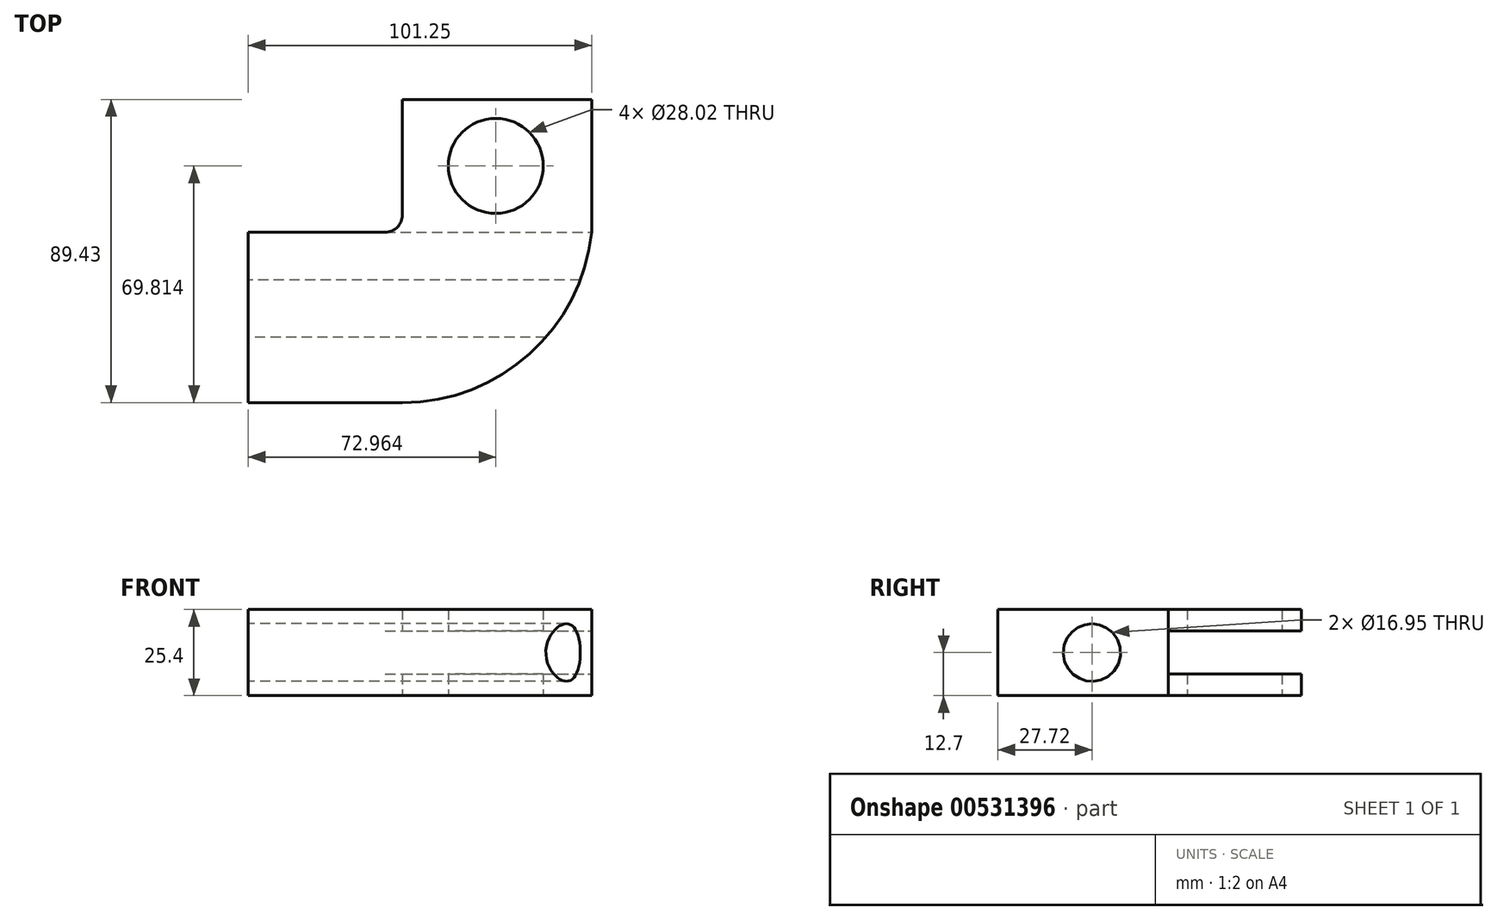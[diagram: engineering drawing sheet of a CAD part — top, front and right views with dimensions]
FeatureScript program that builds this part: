
annotation { "Feature Type Name" : "Feature", "Feature Type Description" : "" }
export const myFeature = defineFeature(function(context is Context, id is Id, definition is map)
    precondition{}
    {
        {
            var Q0;
            Q0=qCreatedBy(makeId("Top.planeOp"),FACE);
            var sketch = newSketch(context, id + "F0", { "sketchPlane" : qUnion([Q0])});
            skLineSegment(sketch, "E0.bottom", {"start": v(-45.45, 22.54) * mm, "end": v(0, 22.54) * mm});
            skLineSegment(sketch, "E0.top", {"start": v(-45.45, -27.72) * mm, "end": v(0, -27.72) * mm});
            skLineSegment(sketch, "E0.left", {"start": v(-45.45, 22.54) * mm, "end": v(-45.45, -27.72) * mm});
            skLineSegment(sketch, "E1.top", {"start": v(0, 61.71) * mm, "end": v(55.8, 61.71) * mm});
            skLineSegment(sketch, "E1.left", {"start": v(0, 22.54) * mm, "end": v(0, 61.71) * mm});
            skLineSegment(sketch, "E1.right", {"start": v(55.8, 22.54) * mm, "end": v(55.8, 61.71) * mm});
            skArc(sketch, "E2", {"start": v(0, -27.72) * mm, "mid": v(37.55, -13.3) * mm, "end": v(55.8, 22.54) * mm});
            skLineSegment(sketch, "E3", {"start": v(0, 22.54) * mm, "end": v(55.8, 22.54) * mm});
            skCircle(sketch, "E4", {"center": v(27.51, 42.1) * mm, "radius": 14 * mm});
            skSolve(sketch);
        }
        {
            var Q0;
            Q0=makeQuery(id+"F0.imprint","IMPRINT",FACE,{"disambiguationData":[TD([[makeQuery(id+"F0.imprint","IMPRINT",EDGE,{"derivedFrom":sQuery(id+"F0.wireOp",EDGE,"E0.bottom")}),-1.0]])]});
            var Q1;
            Q1=makeQuery(id+"F0.imprint","IMPRINT",FACE,{"disambiguationData":[TD([[makeQuery(id+"F0.imprint","IMPRINT",EDGE,{"derivedFrom":sQuery(id+"F0.wireOp",EDGE,"E1.top")}),-1.0]])]});
            extrude(context, id + "F1", {"entities" : qUnion([Q0, Q1]), "endBound" : BoundingType.SYMMETRIC, "depth" : 25.4 * mm, "offsetDistance" : 25.4 * mm});
        }
        {
            var Q0;
            Q0=makeQuery(id+"F0.imprint","IMPRINT",FACE,{"disambiguationData":[TD([[makeQuery(id+"F0.imprint","IMPRINT",EDGE,{"derivedFrom":sQuery(id+"F0.wireOp",EDGE,"E1.top")}),-1.0]])]});
            extrude(context, id + "F2", {"entities" : qUnion([Q0]), "operationType" : NewBodyOperationType.REMOVE, "endBound" : BoundingType.SYMMETRIC, "depth" : 12.7 * mm, "offsetDistance" : 25.4 * mm});
        }
        {
            var Q0;
            {var subQ0=sQuery(id+"F0.wireOp",EDGE,"E4");var subQ1=sQuery(id+"F0.wireOp",EDGE,"E3");var subQ2=sQuery(id+"F0.wireOp",EDGE,"E1.right");var subQ3=sQuery(id+"F0.wireOp",EDGE,"E1.left");var subQ4=sQuery(id+"F0.wireOp",EDGE,"E1.top");var subQ5=sQuery(id+"F0.wireOp",EDGE,"E0.bottom");Q0=makeQuery(id+"F2.boolean.opBoolean","SPLIT",EDGE,{"disambiguationData":[TD([makeQuery(id+"F2.opExtrude","CAP_FACE",FACE,{"disambiguationData":[OSD([subQ4,subQ3,subQ2,subQ1,subQ0])],"isStart":false})])],"derivedFrom":makeQuery(id+"F1.opExtrude","SWEPT_EDGE",EDGE,{"disambiguationData":[OSD([subQ5,subQ3,subQ1])]})});}
            fillet(context, id + "F3", {"entities" : qUnion([Q0]), "radius" : 5.08 * mm, "tangentPropagation" : true, "allowEdgeOverflow" : false});
        }
        {
            var Q0;
            {var subQ0=sQuery(id+"F0.wireOp",EDGE,"E4");var subQ1=sQuery(id+"F0.wireOp",EDGE,"E3");var subQ2=sQuery(id+"F0.wireOp",EDGE,"E1.right");var subQ3=sQuery(id+"F0.wireOp",EDGE,"E1.left");var subQ4=sQuery(id+"F0.wireOp",EDGE,"E1.top");var subQ5=sQuery(id+"F0.wireOp",EDGE,"E0.bottom");Q0=makeQuery(id+"F2.boolean.opBoolean","SPLIT",EDGE,{"disambiguationData":[TD([makeQuery(id+"F2.opExtrude","CAP_FACE",FACE,{"disambiguationData":[OSD([subQ4,subQ3,subQ2,subQ1,subQ0])],"isStart":true})])],"derivedFrom":makeQuery(id+"F1.opExtrude","SWEPT_EDGE",EDGE,{"disambiguationData":[OSD([subQ5,subQ3,subQ1])]})});}
            fillet(context, id + "F4", {"entities" : qUnion([Q0]), "radius" : 5.08 * mm, "tangentPropagation" : true, "allowEdgeOverflow" : false});
        }
        {
            var Q0;
            Q0=makeQuery(id+"F1.opExtrude","SWEPT_FACE",FACE,{"disambiguationData":[OSD([sQuery(id+"F0.wireOp",EDGE,"E0.left")])]});
            var sketch = newSketch(context, id + "F5", { "sketchPlane" : qUnion([Q0])});
            skCircle(sketch, "E5", {"center": v(0, 0) * mm, "radius": 8.48 * mm});
            skSolve(sketch);
        }
        {
            var Q0;
            Q0=makeQuery(id+"F5.imprint","IMPRINT",FACE,{"disambiguationData":[TD([[makeQuery(id+"F5.imprint","IMPRINT",EDGE,{"derivedFrom":sQuery(id+"F5.wireOp",EDGE,"E5")}),1.0]])]});
            extrude(context, id + "F6", {"entities" : qUnion([Q0]), "operationType" : NewBodyOperationType.REMOVE, "oppositeDirection" : true, "depth" : 125.95 * mm, "offsetDistance" : 25.4 * mm});
        }
    });
